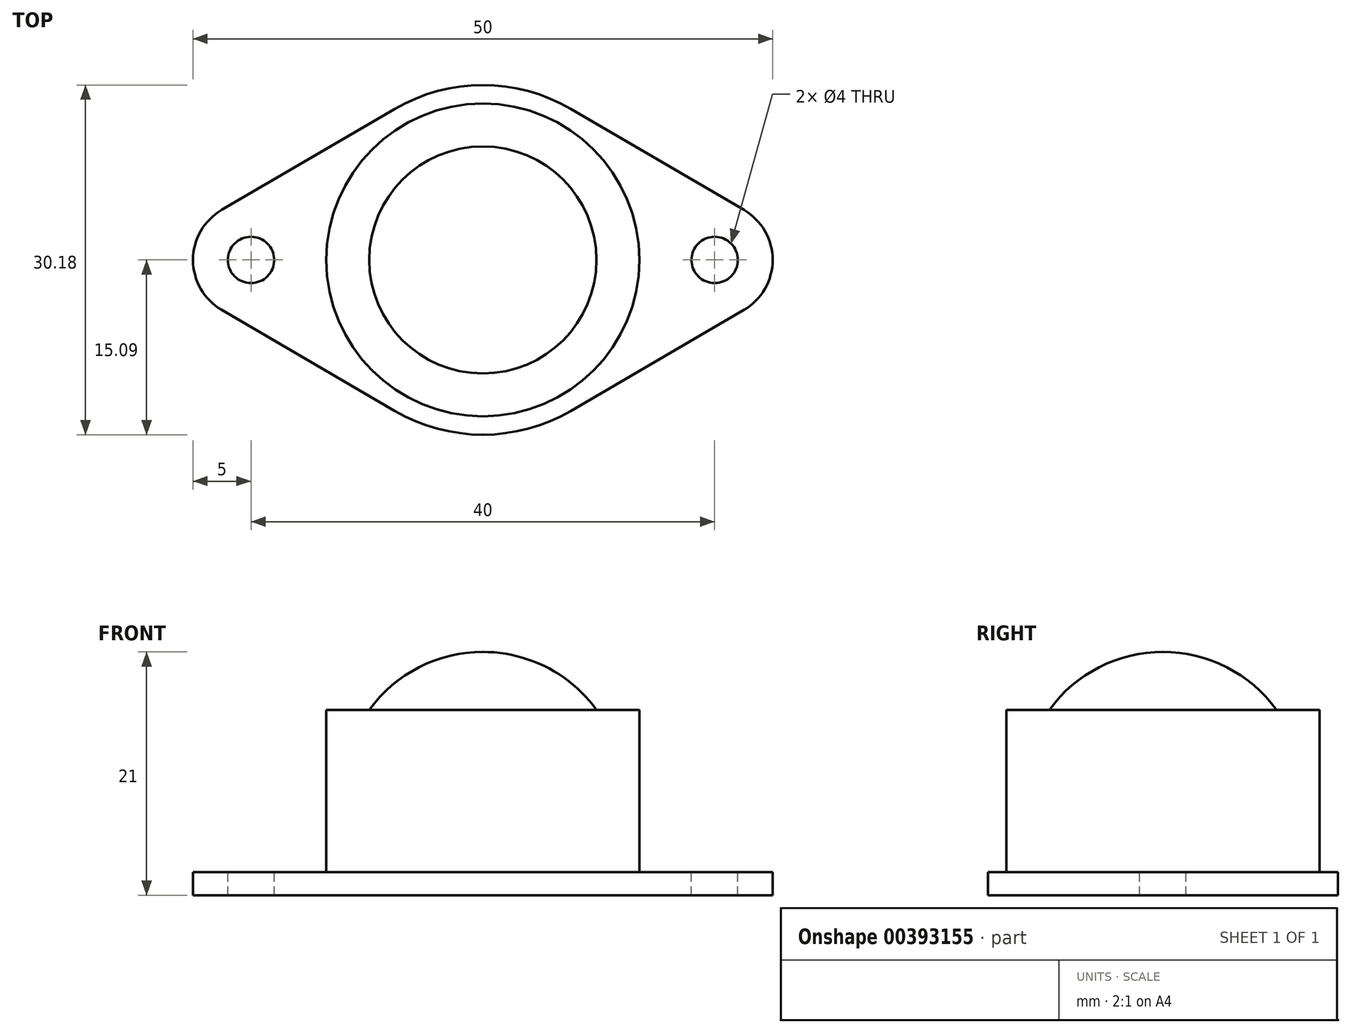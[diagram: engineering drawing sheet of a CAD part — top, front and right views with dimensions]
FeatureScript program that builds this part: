
annotation { "Feature Type Name" : "Feature", "Feature Type Description" : "" }
export const myFeature = defineFeature(function(context is Context, id is Id, definition is map)
    precondition{}
    {
        {
            var Q0;
            Q0=qCreatedBy(makeId("Front.planeOp"),FACE);
            var sketch = newSketch(context, id + "F0", { "sketchPlane" : qUnion([Q0])});
            skLineSegment(sketch, "E0", {"start": v(0, 0) * mm, "end": v(0, 28.14) * mm, "construction": true});
            skArc(sketch, "E1", {"start": v(9.8, 16) * mm, "mid": v(5.5, 19.68) * mm, "end": v(0, 21) * mm});
            skLineSegment(sketch, "E2", {"start": v(9.8, 16) * mm, "end": v(13.5, 16) * mm});
            skLineSegment(sketch, "E3", {"start": v(13.5, 16) * mm, "end": v(13.5, 2) * mm});
            skLineSegment(sketch, "E4", {"start": v(13.5, 2) * mm, "end": v(25, 2) * mm});
            skLineSegment(sketch, "E5", {"start": v(25, 2) * mm, "end": v(25, 0) * mm});
            skLineSegment(sketch, "E6", {"start": v(25, 0) * mm, "end": v(0, 0) * mm});
            skPoint(sketch, "E7.orphan", {"position": v(8.2, 0) * mm});
            skLineSegment(sketch, "E8", {"start": v(0, 21) * mm, "end": v(0, 0) * mm});
            skSolve(sketch);
        }
        {
            var Q0;
            Q0=makeQuery(id+"F0.imprint","IMPRINT",FACE,{"disambiguationData":[TD([[makeQuery(id+"F0.imprint","IMPRINT",EDGE,{"derivedFrom":sQuery(id+"F0.wireOp",EDGE,"E1")}),1.0]])]});
            var Q1;
            Q1=sQuery(id+"F0.wireOp",EDGE,"E8");
            revolve(context, id + "F1", {"entities" : qUnion([Q0]), "axis" : qUnion([Q1]), "revolveType" : RevolveType.FULL});
        }
        {
            var Q0;
            Q0=makeQuery(id+"F1.opRevolve","SWEPT_FACE",FACE,{"disambiguationData":[OSD([sQuery(id+"F0.wireOp",EDGE,"E4")])]});
            var sketch = newSketch(context, id + "F2", { "sketchPlane" : qUnion([Q0])});
            skCircle(sketch, "E9", {"center": v(-20, 0) * mm, "radius": 2 * mm});
            skCircle(sketch, "E10", {"center": v(20, 0) * mm, "radius": 2 * mm});
            skArc(sketch, "E11", {"start": v(-22.52, 4.32) * mm, "mid": v(-24.34, 2.49) * mm, "end": v(-25, 0) * mm});
            skLineSegment(sketch, "E12", {"start": v(-7.6, 13.03) * mm, "end": v(-22.52, 4.32) * mm});
            skLineSegment(sketch, "E13", {"start": v(0, 15.09) * mm, "end": v(0, 0) * mm, "construction": true});
            skLineSegment(sketch, "E14", {"start": v(0, 0) * mm, "end": v(-35.77, 0) * mm, "construction": true});
            skArc(sketch, "E15", {"start": v(0, 15.09) * mm, "mid": v(-3.94, 14.56) * mm, "end": v(-7.6, 13.03) * mm});
            skPoint(sketch, "E16.orphan", {"position": v(0, 17.47) * mm});
            skArc(sketch, "E17.MirrorCS", {"start": v(-22.52, -4.32) * mm, "mid": v(-24.34, -2.49) * mm, "end": v(-25, 0) * mm});
            skLineSegment(sketch, "E18.MirrorCS", {"start": v(-7.6, -13.03) * mm, "end": v(-22.52, -4.32) * mm});
            skArc(sketch, "E19.MirrorCS", {"start": v(0, -15.09) * mm, "mid": v(-3.94, -14.56) * mm, "end": v(-7.6, -13.03) * mm});
            skArc(sketch, "E20.MirrorCS", {"start": v(0, 15.09) * mm, "mid": v(3.94, 14.56) * mm, "end": v(7.6, 13.03) * mm});
            skLineSegment(sketch, "E21.MirrorCS", {"start": v(7.6, 13.03) * mm, "end": v(22.52, 4.32) * mm});
            skArc(sketch, "E22.MirrorCS", {"start": v(22.52, 4.32) * mm, "mid": v(24.34, 2.49) * mm, "end": v(25, 0) * mm});
            skArc(sketch, "E23.MirrorCS", {"start": v(22.52, -4.32) * mm, "mid": v(24.34, -2.49) * mm, "end": v(25, 0) * mm});
            skLineSegment(sketch, "E24.MirrorCS", {"start": v(7.6, -13.03) * mm, "end": v(22.52, -4.32) * mm});
            skArc(sketch, "E25.MirrorCS", {"start": v(0, -15.09) * mm, "mid": v(3.94, -14.56) * mm, "end": v(7.6, -13.03) * mm});
            skCircle(sketch, "E26", {"center": v(0, 0) * mm, "radius": 29.92 * mm});
            skSolve(sketch);
        }
        {
            var Q0;
            Q0 = qSketchRegion(id + "F2", true);
            var Q1;
            Q1=makeQuery(id+"F2.imprint","IMPRINT",FACE,{"disambiguationData":[TD([[makeQuery(id+"F2.imprint","IMPRINT",EDGE,{"derivedFrom":sQuery(id+"F2.wireOp",EDGE,"E9")}),1.0]])]});
            var Q2;
            Q2=makeQuery(id+"F2.imprint","IMPRINT",FACE,{"disambiguationData":[TD([[makeQuery(id+"F2.imprint","IMPRINT",EDGE,{"derivedFrom":sQuery(id+"F2.wireOp",EDGE,"E10")}),1.0]])]});
            extrude(context, id + "F3", {"entities" : qUnion([Q0, Q1, Q2]), "operationType" : NewBodyOperationType.REMOVE, "endBound" : BoundingType.THROUGH_ALL, "oppositeDirection" : true, "depth" : 25.4 * mm});
        }
    });
